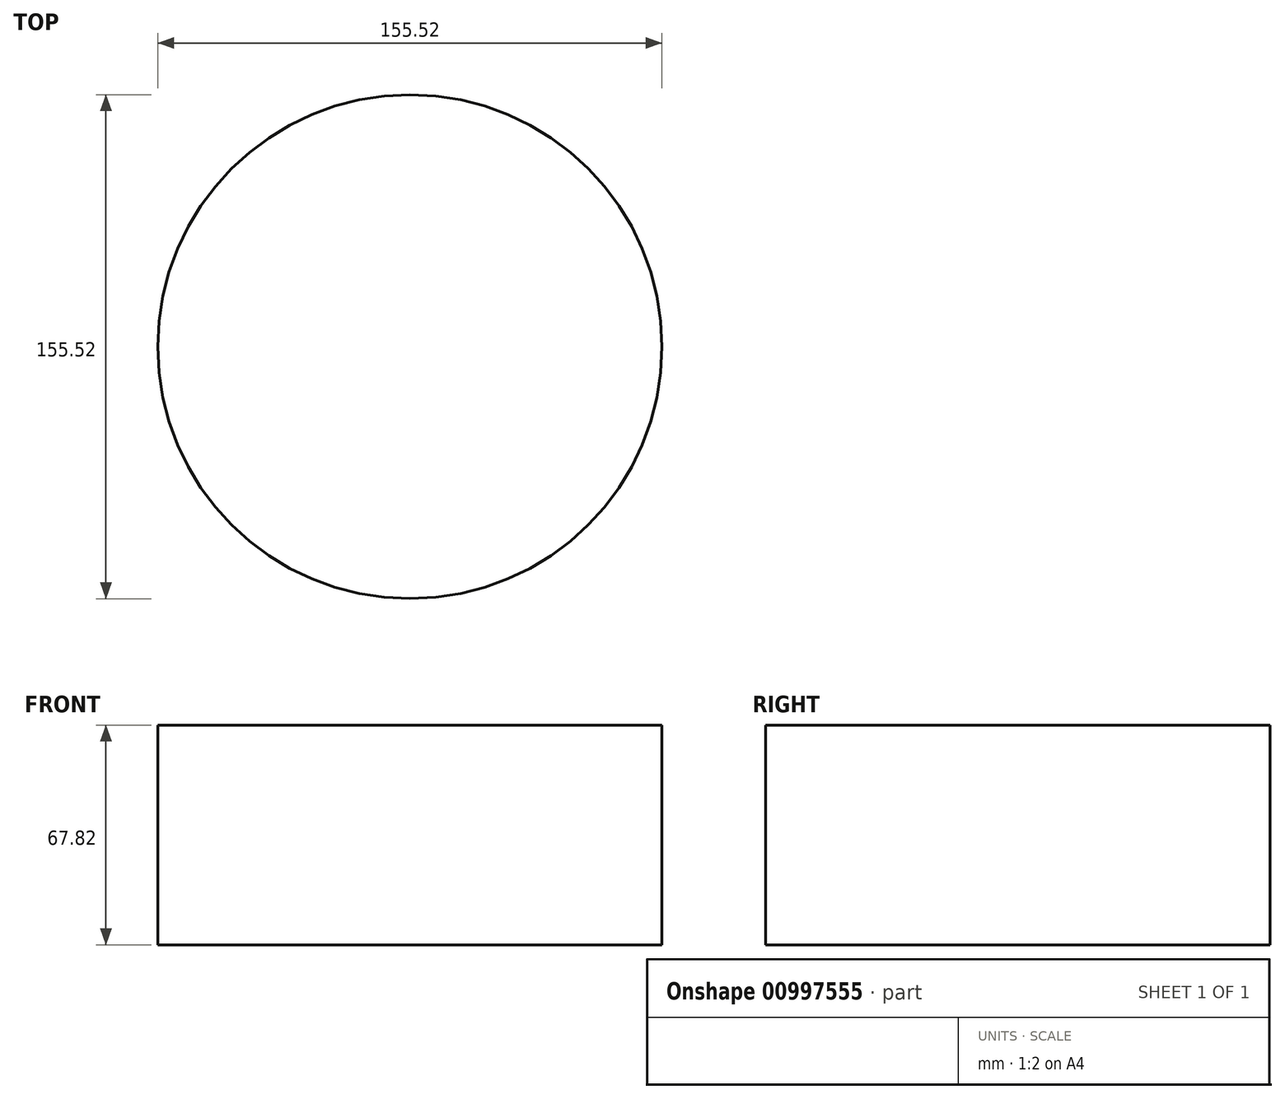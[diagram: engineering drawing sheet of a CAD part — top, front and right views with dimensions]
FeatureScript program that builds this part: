
annotation { "Feature Type Name" : "Feature", "Feature Type Description" : "" }
export const myFeature = defineFeature(function(context is Context, id is Id, definition is map)
    precondition{}
    {
        {
            var Q0;
            Q0=qCreatedBy(makeId("Top.planeOp"),FACE);
            var sketch = newSketch(context, id + "F0", { "sketchPlane" : qUnion([Q0])});
            skCircle(sketch, "E0", {"center": v(0, 0) * mm, "radius": 77.76 * mm});
            skSolve(sketch);
        }
        {
            var Q0;
            Q0=makeQuery(id+"F0.imprint","IMPRINT",FACE,{"disambiguationData":[TD([[makeQuery(id+"F0.imprint","IMPRINT",EDGE,{"derivedFrom":sQuery(id+"F0.wireOp",EDGE,"E0")}),1.0]])]});
            extrude(context, id + "F1", {"entities" : qUnion([Q0]), "depth" : 67.82 * mm, "offsetDistance" : 25.4 * mm});
        }
    });
